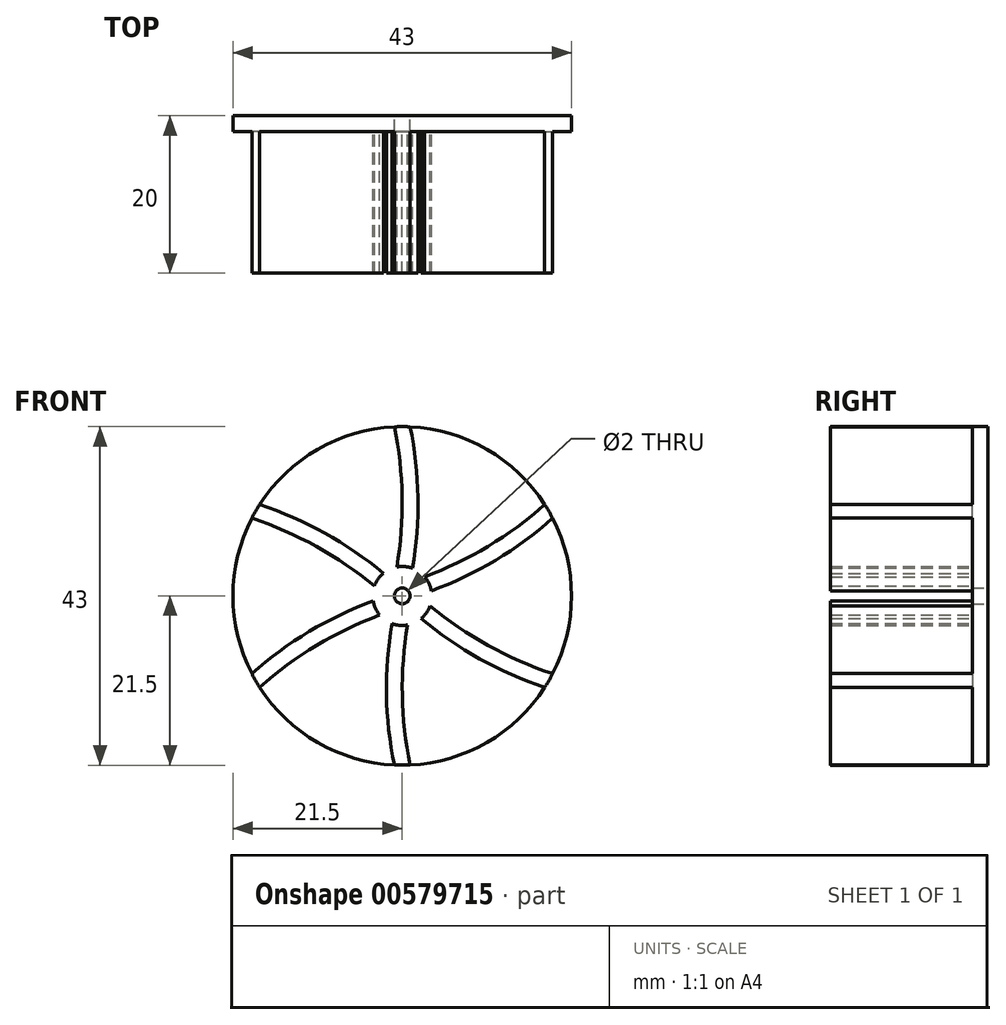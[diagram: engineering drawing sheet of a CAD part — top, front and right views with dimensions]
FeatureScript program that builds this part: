
annotation { "Feature Type Name" : "Feature", "Feature Type Description" : "" }
export const myFeature = defineFeature(function(context is Context, id is Id, definition is map)
    precondition{}
    {
        {
            var Q0;
            Q0=qCreatedBy(makeId("Front.planeOp"),FACE);
            var sketch = newSketch(context, id + "F0", { "sketchPlane" : qUnion([Q0])});
            skCircle(sketch, "E0", {"center": v(0, 0) * mm, "radius": 21.5 * mm});
            skSolve(sketch);
        }
        {
            var Q0;
            Q0 = qSketchRegion(id + "F0", true);
            extrude(context, id + "F1", {"entities" : qUnion([Q0]), "depth" : 2 * mm, "offsetDistance" : 25.4 * mm});
        }
        {
            var Q0;
            Q0=makeQuery(id+"F1.opExtrude","CAP_FACE",FACE,{"disambiguationData":[OSD([sQuery(id+"F0.wireOp",EDGE,"E0")])],"isStart":true});
            var sketch = newSketch(context, id + "F2", { "sketchPlane" : qUnion([Q0])});
            skLineSegment(sketch, "E1", {"start": v(0, 0) * mm, "end": v(0, 21.5) * mm});
            skLineSegment(sketch, "E2", {"start": v(0, 21.5) * mm, "end": v(0, -21.5) * mm, "construction": true});
            skLineSegment(sketch, "E3", {"start": v(0, 0) * mm, "end": v(-18.62, 10.75) * mm, "construction": true});
            skLineSegment(sketch, "E4", {"start": v(0, 0) * mm, "end": v(-18.62, -10.75) * mm, "construction": true});
            skLineSegment(sketch, "E5.MirrorCS", {"start": v(0, 0) * mm, "end": v(18.62, 10.75) * mm, "construction": true});
            skLineSegment(sketch, "E6.MirrorCS", {"start": v(0, 0) * mm, "end": v(18.62, -10.75) * mm, "construction": true});
            skCircle(sketch, "E7", {"center": v(0, 0) * mm, "radius": 2 * mm});
            skLineSegment(sketch, "E8", {"start": v(-1.73, 1) * mm, "end": v(-1.15, 2) * mm});
            skLineSegment(sketch, "E9", {"start": v(-1.15, 2) * mm, "end": v(-2.3, 0) * mm});
            skLineSegment(sketch, "E10", {"start": v(0, 2) * mm, "end": v(-1.15, 2) * mm});
            skLineSegment(sketch, "E11", {"start": v(-1.15, 2) * mm, "end": v(1.15, 2) * mm});
            skLineSegment(sketch, "E12", {"start": v(1.73, 1) * mm, "end": v(1.15, 2) * mm});
            skLineSegment(sketch, "E13", {"start": v(1.15, 2) * mm, "end": v(2.3, 0) * mm});
            skLineSegment(sketch, "E14", {"start": v(1.73, -1) * mm, "end": v(1.15, -2) * mm});
            skLineSegment(sketch, "E15", {"start": v(1.15, -2) * mm, "end": v(2.3, 0) * mm});
            skLineSegment(sketch, "E16", {"start": v(0, -2) * mm, "end": v(1.15, -2) * mm});
            skLineSegment(sketch, "E17", {"start": v(1.15, -2) * mm, "end": v(-1.15, -2) * mm});
            skLineSegment(sketch, "E18", {"start": v(-1.73, -1) * mm, "end": v(-2.3, 0) * mm});
            skLineSegment(sketch, "E19", {"start": v(-2.3, 0) * mm, "end": v(-1.15, -2) * mm});
            skPoint(sketch, "E20", {"position": v(1, 2) * mm});
            skPoint(sketch, "E21", {"position": v(1.23, 1.87) * mm});
            skPoint(sketch, "E22", {"position": v(-1.23, 1.87) * mm});
            skPoint(sketch, "E23.MirrorP", {"position": v(-1, 2) * mm});
            skPoint(sketch, "E24.MirrorP", {"position": v(-2.23, 0.13) * mm});
            skPoint(sketch, "E25", {"position": v(-2.23, -0.13) * mm});
            skPoint(sketch, "E26.MirrorP", {"position": v(-1.23, -1.87) * mm});
            skPoint(sketch, "E27.MirrorP", {"position": v(-1, -2) * mm});
            skPoint(sketch, "E28.MirrorP", {"position": v(1, -2) * mm});
            skPoint(sketch, "E29.MirrorP", {"position": v(2.23, 0.13) * mm});
            skPoint(sketch, "E30.MirrorP", {"position": v(2.23, -0.13) * mm});
            skLineSegment(sketch, "E31", {"start": v(1.23, 1.87) * mm, "end": v(18.1, 11.6) * mm, "construction": true});
            skLineSegment(sketch, "E32", {"start": v(2.23, 0.13) * mm, "end": v(19.1, 9.87) * mm, "construction": true});
            skPoint(sketch, "E33", {"position": v(9.67, 6.74) * mm});
            skPoint(sketch, "E34", {"position": v(10.67, 5) * mm});
            skLineSegment(sketch, "E35", {"start": v(9.67, 6.74) * mm, "end": v(10.67, 5) * mm, "construction": true});
            skPoint(sketch, "E36", {"position": v(10.17, 5.87) * mm});
            skArc(sketch, "E37", {"start": v(1.23, 1.87) * mm, "mid": v(10.17, 5.87) * mm, "end": v(18.1, 11.6) * mm});
            skLineSegment(sketch, "E38.MirrorCS", {"start": v(11.67, 3.27) * mm, "end": v(10.67, 5) * mm, "construction": true});
            skPoint(sketch, "E39.MirrorP", {"position": v(11.17, 4.14) * mm});
            skArc(sketch, "E40", {"start": v(2.23, 0.13) * mm, "mid": v(11.17, 4.14) * mm, "end": v(19.1, 9.87) * mm});
            skLineSegment(sketch, "E41", {"start": v(2.23, -0.13) * mm, "end": v(19.1, -9.87) * mm, "construction": true});
            skPoint(sketch, "E42", {"position": v(1.23, -1.87) * mm});
            skLineSegment(sketch, "E43", {"start": v(1.23, -1.87) * mm, "end": v(18.1, -11.6) * mm, "construction": true});
            skPoint(sketch, "E44", {"position": v(9.67, -6.74) * mm});
            skPoint(sketch, "E45", {"position": v(10.67, -5) * mm});
            skLineSegment(sketch, "E46", {"start": v(10.67, -5) * mm, "end": v(9.67, -6.74) * mm, "construction": true});
            skLineSegment(sketch, "E47.MirrorCS", {"start": v(8.67, -8.47) * mm, "end": v(9.67, -6.74) * mm, "construction": true});
            skPoint(sketch, "E48", {"position": v(10.17, -5.87) * mm});
            skPoint(sketch, "E49", {"position": v(9.17, -7.6) * mm});
            skArc(sketch, "E50", {"start": v(2.23, -0.13) * mm, "mid": v(10.17, -5.87) * mm, "end": v(19.1, -9.87) * mm});
            skArc(sketch, "E51", {"start": v(1.23, -1.87) * mm, "mid": v(9.17, -7.6) * mm, "end": v(18.1, -11.6) * mm});
            skLineSegment(sketch, "E52", {"start": v(-1, 2) * mm, "end": v(-1, 21.48) * mm, "construction": true});
            skLineSegment(sketch, "E53", {"start": v(1, 2) * mm, "end": v(1, 21.48) * mm, "construction": true});
            skPoint(sketch, "E54", {"position": v(-1, 11.74) * mm});
            skPoint(sketch, "E55", {"position": v(1, 11.74) * mm});
            skLineSegment(sketch, "E56", {"start": v(-1, 11.74) * mm, "end": v(1, 11.74) * mm, "construction": true});
            skPoint(sketch, "E57", {"position": v(0, 11.74) * mm});
            skLineSegment(sketch, "E58.MirrorCS", {"start": v(3, 11.74) * mm, "end": v(1, 11.74) * mm, "construction": true});
            skPoint(sketch, "E59.MirrorP", {"position": v(2, 11.74) * mm});
            skArc(sketch, "E60", {"start": v(-1, 2) * mm, "mid": v(0, 11.74) * mm, "end": v(-1, 21.48) * mm});
            skArc(sketch, "E61", {"start": v(1, 2) * mm, "mid": v(2, 11.74) * mm, "end": v(1, 21.48) * mm});
            skLineSegment(sketch, "E62", {"start": v(-1, -2) * mm, "end": v(-1, -21.48) * mm, "construction": true});
            skLineSegment(sketch, "E63", {"start": v(1, -2) * mm, "end": v(1, -21.48) * mm, "construction": true});
            skPoint(sketch, "E64", {"position": v(-1, -11.74) * mm});
            skPoint(sketch, "E65", {"position": v(1, -11.74) * mm});
            skLineSegment(sketch, "E66", {"start": v(-1, -11.74) * mm, "end": v(1, -11.74) * mm, "construction": true});
            skPoint(sketch, "E67", {"position": v(0, -11.74) * mm});
            skLineSegment(sketch, "E68.MirrorCS", {"start": v(-1, -11.74) * mm, "end": v(-3, -11.74) * mm, "construction": true});
            skPoint(sketch, "E69.MirrorP", {"position": v(-2, -11.74) * mm});
            skArc(sketch, "E70", {"start": v(1, -2) * mm, "mid": v(0, -11.74) * mm, "end": v(1, -21.48) * mm});
            skArc(sketch, "E71", {"start": v(-1, -2) * mm, "mid": v(-2, -11.74) * mm, "end": v(-1, -21.48) * mm});
            skLineSegment(sketch, "E72", {"start": v(-2.23, -0.13) * mm, "end": v(-19.1, -9.87) * mm, "construction": true});
            skLineSegment(sketch, "E73", {"start": v(-1.23, -1.87) * mm, "end": v(-18.1, -11.6) * mm, "construction": true});
            skPoint(sketch, "E74", {"position": v(-10.67, -5) * mm});
            skPoint(sketch, "E75", {"position": v(-9.67, -6.74) * mm});
            skLineSegment(sketch, "E76", {"start": v(-10.67, -5) * mm, "end": v(-9.67, -6.74) * mm, "construction": true});
            skPoint(sketch, "E77", {"position": v(-10.17, -5.87) * mm});
            skLineSegment(sketch, "E78.MirrorCS", {"start": v(-10.67, -5) * mm, "end": v(-11.67, -3.27) * mm, "construction": true});
            skPoint(sketch, "E79.MirrorP", {"position": v(-11.17, -4.14) * mm});
            skArc(sketch, "E80", {"start": v(-1.23, -1.87) * mm, "mid": v(-10.17, -5.87) * mm, "end": v(-18.1, -11.6) * mm});
            skArc(sketch, "E81", {"start": v(-2.23, -0.13) * mm, "mid": v(-11.17, -4.14) * mm, "end": v(-19.1, -9.87) * mm});
            skLineSegment(sketch, "E82", {"start": v(-2.23, 0.13) * mm, "end": v(-19.1, 9.87) * mm, "construction": true});
            skLineSegment(sketch, "E83", {"start": v(-1.23, 1.87) * mm, "end": v(-18.1, 11.6) * mm, "construction": true});
            skPoint(sketch, "E84", {"position": v(-9.67, 6.74) * mm});
            skPoint(sketch, "E85", {"position": v(-10.67, 5) * mm});
            skLineSegment(sketch, "E86", {"start": v(-9.67, 6.74) * mm, "end": v(-10.67, 5) * mm, "construction": true});
            skPoint(sketch, "E87", {"position": v(-10.17, 5.87) * mm});
            skLineSegment(sketch, "E88.MirrorCS", {"start": v(-9.67, 6.74) * mm, "end": v(-8.67, 8.47) * mm, "construction": true});
            skPoint(sketch, "E89.MirrorP", {"position": v(-9.17, 7.6) * mm});
            skArc(sketch, "E90", {"start": v(-1.23, 1.87) * mm, "mid": v(-9.17, 7.6) * mm, "end": v(-18.1, 11.6) * mm});
            skArc(sketch, "E91", {"start": v(-2.23, 0.13) * mm, "mid": v(-10.17, 5.87) * mm, "end": v(-19.1, 9.87) * mm});
            skSolve(sketch);
        }
        {
            var Q0;
            {var subQ3=sQuery(id+"F2.wireOp",EDGE,"E37");Q0=makeQuery(id+"F2.imprint","IMPRINT",FACE,{"disambiguationData":[TD([[makeQuery(id+"F2.imprint","IMPRINT",EDGE,{"derivedFrom":subQ3}),-1.0]])]});}
            var Q1;
            {var subQ0=sQuery(id+"F2.wireOp",EDGE,"E61");Q1=makeQuery(id+"F2.imprint","IMPRINT",FACE,{"disambiguationData":[TD([[makeQuery(id+"F2.imprint","IMPRINT",EDGE,{"derivedFrom":subQ0}),1.0]])]});}
            var Q2;
            {var subQ0=sQuery(id+"F2.wireOp",EDGE,"E60");var subQ3=sQuery(id+"F2.wireOp",EDGE,"E11");var subQ5=makeQuery(id+"F2.imprint","INTERSECT",VERTEX,{"derivedFrom":[subQ3,subQ0]});Q2=makeQuery(id+"F2.imprint","IMPRINT",FACE,{"disambiguationData":[TD([[makeQuery(id+"F2.imprint","IMPRINT",EDGE,{"disambiguationData":[TD([[subQ5,-1.0]])],"derivedFrom":subQ0}),-1.0]])]});}
            var Q3;
            {var subQ0=sQuery(id+"F2.wireOp",EDGE,"E90");Q3=makeQuery(id+"F2.imprint","IMPRINT",FACE,{"disambiguationData":[TD([[makeQuery(id+"F2.imprint","IMPRINT",EDGE,{"derivedFrom":subQ0}),1.0]])]});}
            var Q4;
            {var subQ1=sQuery(id+"F2.wireOp",EDGE,"E80");Q4=makeQuery(id+"F2.imprint","IMPRINT",FACE,{"disambiguationData":[TD([[makeQuery(id+"F2.imprint","IMPRINT",EDGE,{"derivedFrom":subQ1}),-1.0]])]});}
            var Q5;
            {var subQ0=sQuery(id+"F2.wireOp",EDGE,"E70");Q5=makeQuery(id+"F2.imprint","IMPRINT",FACE,{"disambiguationData":[TD([[makeQuery(id+"F2.imprint","IMPRINT",EDGE,{"derivedFrom":subQ0}),-1.0]])]});}
            var Q6;
            {var subQ1=sQuery(id+"F2.wireOp",EDGE,"E50");Q6=makeQuery(id+"F2.imprint","IMPRINT",FACE,{"disambiguationData":[TD([[makeQuery(id+"F2.imprint","IMPRINT",EDGE,{"derivedFrom":subQ1}),-1.0]])]});}
            var Q7;
            {var subQ0=sQuery(id+"F2.wireOp",EDGE,"E1");var subQ1=makeQuery(id+"F1.opExtrude","CAP_EDGE",EDGE,{"disambiguationData":[OSD([sQuery(id+"F0.wireOp",EDGE,"E0")])],"isStart":true});var subQ2=makeQuery(id+"F2.imprint","INTERSECT",VERTEX,{"derivedFrom":[subQ1,subQ0]});Q7=makeQuery(id+"F2.imprint","IMPRINT",FACE,{"disambiguationData":[TD([[makeQuery(id+"F2.imprint","IMPRINT",EDGE,{"disambiguationData":[TD([[subQ2,1.0]])],"derivedFrom":subQ0}),1.0]])]});}
            extrude(context, id + "F3", {"entities" : qUnion([Q0, Q1, Q2, Q3, Q4, Q5, Q6, Q7]), "operationType" : NewBodyOperationType.ADD, "depth" : 18 * mm, "offsetDistance" : 25.4 * mm});
        }
        {
            var Q0;
            Q0=makeQuery(id+"F1.opExtrude","CAP_FACE",FACE,{"disambiguationData":[OSD([sQuery(id+"F0.wireOp",EDGE,"E0")])],"isStart":false});
            var sketch = newSketch(context, id + "F4", { "sketchPlane" : qUnion([Q0])});
            skCircle(sketch, "E92", {"center": v(0, 0) * mm, "radius": 1 * mm});
            skSolve(sketch);
        }
        {
            var Q0;
            Q0 = qSketchRegion(id + "F4", true);
            extrude(context, id + "F5", {"entities" : qUnion([Q0]), "operationType" : NewBodyOperationType.REMOVE, "oppositeDirection" : true, "depth" : 25.4 * mm, "offsetDistance" : 25.4 * mm});
        }
        {
            var Q0;
            Q0=makeQuery(id+"F1.opExtrude","CAP_FACE",FACE,{"disambiguationData":[OSD([sQuery(id+"F0.wireOp",EDGE,"E0")])],"isStart":true});
            var sketch = newSketch(context, id + "F6", { "sketchPlane" : qUnion([Q0])});
            skCircle(sketch, "E93", {"center": v(0, 0) * mm, "radius": 3.75 * mm});
            skSolve(sketch);
        }
        {
            var Q0;
            Q0 = qSketchRegion(id + "F6", true);
            extrude(context, id + "F7", {"entities" : qUnion([Q0]), "operationType" : NewBodyOperationType.REMOVE, "depth" : 25.4 * mm, "offsetDistance" : 25.4 * mm});
        }
        {
            var Q0;
            Q0=qCreatedBy(makeId("Front.planeOp"),FACE);
            var sketch = newSketch(context, id + "F8", { "sketchPlane" : qUnion([Q0])});
            skLineSegment(sketch, "E94", {"start": v(0, 49.21) * mm, "end": v(0, -51.52) * mm});
            skSolve(sketch);
        }
        {
            var Q0;
            Q0=makeQuery(id+"F1.opExtrude","SWEPT_BODY",BODY,{"disambiguationData":[OSD([sQuery(id+"F0.wireOp",EDGE,"E0")])]});
            var Q1;
            Q1=sQuery(id+"F8.wireOp",EDGE,"E94");
            transform(context, id + "F9", {"entities" : qUnion([Q0]), "transformType" : TransformType.ROTATION, "transformAxis" : qUnion([Q1]), "angle" : 180 * degree, "makeCopy" : false});
        }
    });
